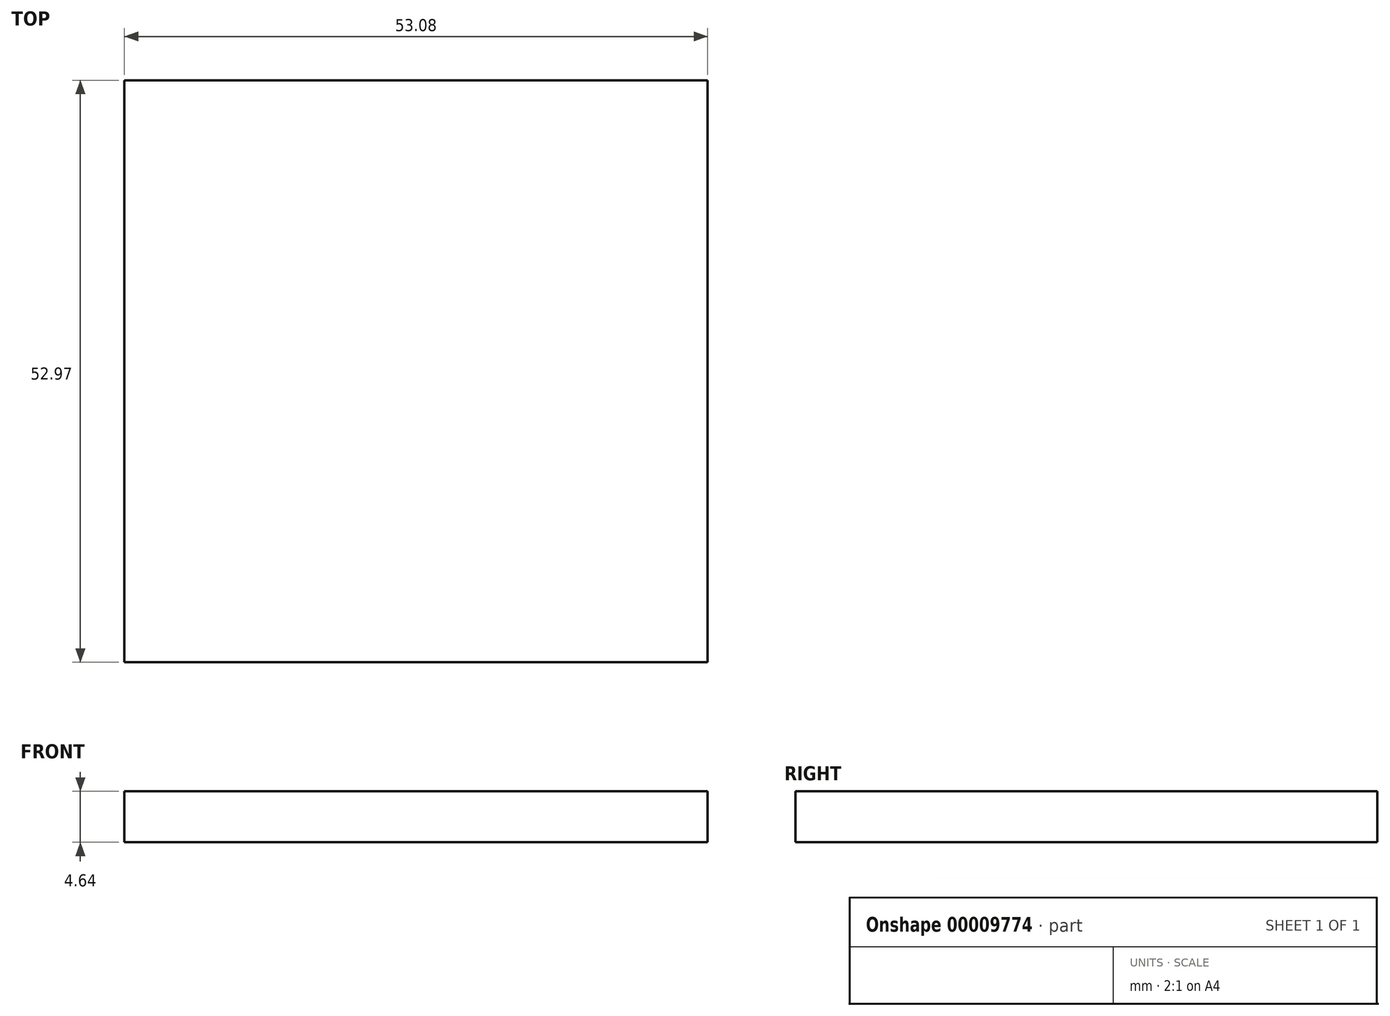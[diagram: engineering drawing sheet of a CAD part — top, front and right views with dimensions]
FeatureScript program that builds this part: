
annotation { "Feature Type Name" : "Feature", "Feature Type Description" : "" }
export const myFeature = defineFeature(function(context is Context, id is Id, definition is map)
    precondition{}
    {
        {
            var Q0;
            Q0=qCreatedBy(makeId("Top.planeOp"),FACE);
            var sketch = newSketch(context, id + "F0", { "sketchPlane" : qUnion([Q0])});
            skLineSegment(sketch, "E0.bottom", {"start": v(0, 0) * mm, "end": v(53.08, 0) * mm});
            skLineSegment(sketch, "E0.top", {"start": v(0, -52.97) * mm, "end": v(53.08, -52.97) * mm});
            skLineSegment(sketch, "E0.left", {"start": v(0, 0) * mm, "end": v(0, -52.97) * mm});
            skLineSegment(sketch, "E0.right", {"start": v(53.08, 0) * mm, "end": v(53.08, -52.97) * mm});
            skSolve(sketch);
        }
        {
            var Q0;
            Q0 = qSketchRegion(id + "F0", true);
            extrude(context, id + "F1", {"entities" : qUnion([Q0]), "depth" : 4.64 * mm});
        }
    });
